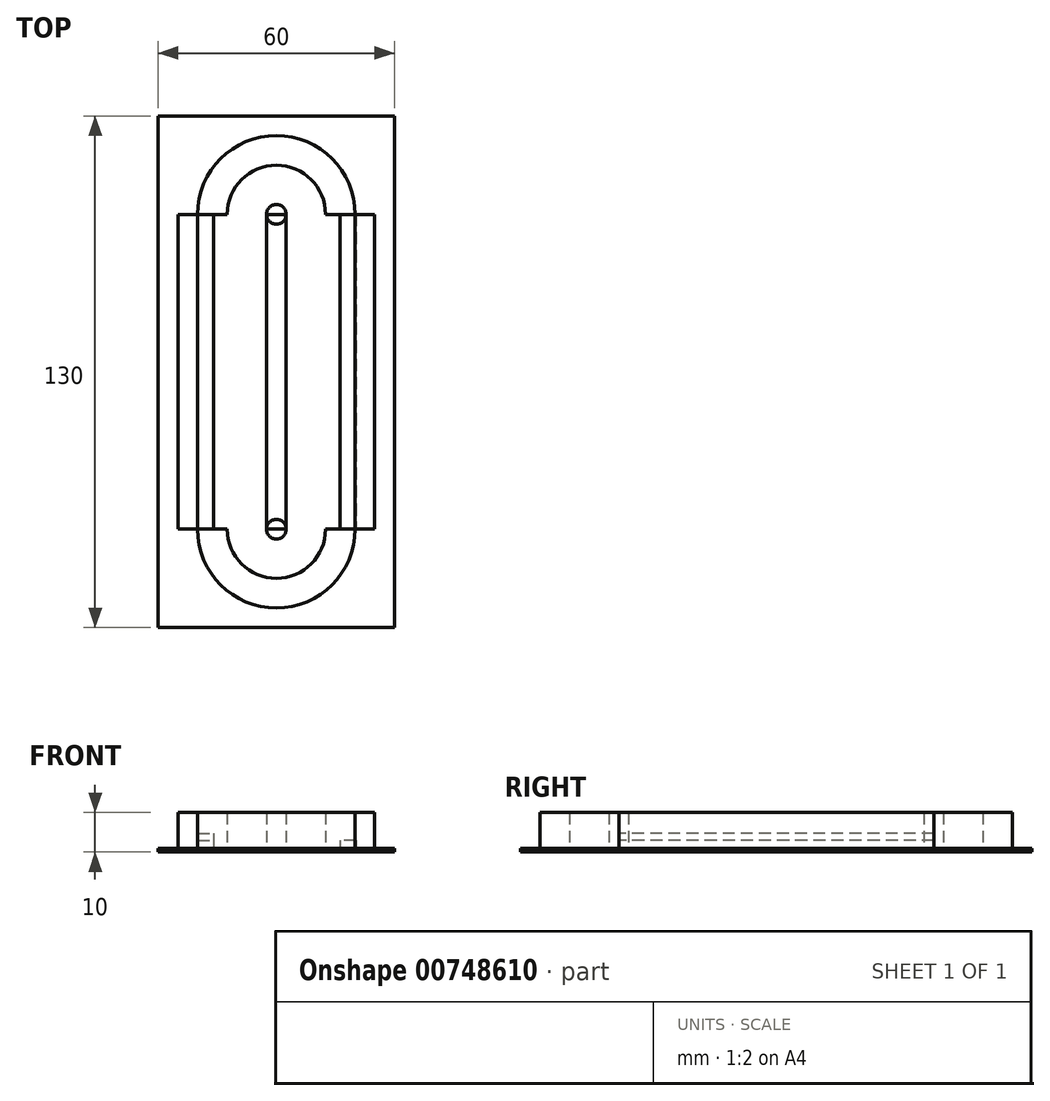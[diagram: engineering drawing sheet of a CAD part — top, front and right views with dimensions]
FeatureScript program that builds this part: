
annotation { "Feature Type Name" : "Feature", "Feature Type Description" : "" }
export const myFeature = defineFeature(function(context is Context, id is Id, definition is map)
    precondition{}
    {
        {
            var Q0;
            Q0=qCreatedBy(makeId("Top.planeOp"),FACE);
            var sketch = newSketch(context, id + "F0", { "sketchPlane" : qUnion([Q0])});
            skLineSegment(sketch, "E0", {"start": v(0, 0) * mm, "end": v(0, 40) * mm});
            skLineSegment(sketch, "E1", {"start": v(0, 40) * mm, "end": v(0, -40) * mm});
            skLineSegment(sketch, "E2", {"start": v(0, -40) * mm, "end": v(0, 0) * mm});
            skCircle(sketch, "E3", {"center": v(0, 40) * mm, "radius": 12.5 * mm});
            skCircle(sketch, "E4", {"center": v(0, -40) * mm, "radius": 12.5 * mm});
            skLineSegment(sketch, "E5", {"start": v(0, -40) * mm, "end": v(-12.5, -40) * mm});
            skLineSegment(sketch, "E6", {"start": v(-12.5, -40) * mm, "end": v(12.5, -40) * mm});
            skLineSegment(sketch, "E7", {"start": v(0, 38.18) * mm, "end": v(0, 40) * mm});
            skLineSegment(sketch, "E8", {"start": v(0, 40) * mm, "end": v(12.5, 40) * mm});
            skLineSegment(sketch, "E9", {"start": v(12.5, 40) * mm, "end": v(-12.5, 40) * mm});
            skLineSegment(sketch, "E10", {"start": v(-12.5, 40) * mm, "end": v(-12.5, -40) * mm});
            skLineSegment(sketch, "E11", {"start": v(12.5, -40) * mm, "end": v(12.5, 40) * mm});
            skCircle(sketch, "E12", {"center": v(0, 40) * mm, "radius": 20 * mm});
            skCircle(sketch, "E13", {"center": v(0, -40) * mm, "radius": 20 * mm});
            skLineSegment(sketch, "E14", {"start": v(14.46, -40) * mm, "end": v(20, -40) * mm});
            skLineSegment(sketch, "E15", {"start": v(20, -40) * mm, "end": v(-20, -40) * mm});
            skLineSegment(sketch, "E16", {"start": v(-20, -40) * mm, "end": v(-20, 40) * mm});
            skLineSegment(sketch, "E17", {"start": v(20, -40) * mm, "end": v(20, 40) * mm});
            skLineSegment(sketch, "E18", {"start": v(20, 40) * mm, "end": v(12.5, 40) * mm});
            skLineSegment(sketch, "E19", {"start": v(-12.5, 40) * mm, "end": v(-20, 40) * mm});
            skLineSegment(sketch, "E20", {"start": v(-20, 40) * mm, "end": v(20, 40) * mm});
            skLineSegment(sketch, "E21", {"start": v(20, 40) * mm, "end": v(25, 40) * mm});
            skLineSegment(sketch, "E22", {"start": v(25, 40) * mm, "end": v(25, -40) * mm});
            skLineSegment(sketch, "E23", {"start": v(25, -40) * mm, "end": v(20, -40) * mm});
            skLineSegment(sketch, "E24", {"start": v(-20, -40) * mm, "end": v(-25, -40) * mm});
            skLineSegment(sketch, "E25", {"start": v(-25, -40) * mm, "end": v(-25, 40) * mm});
            skLineSegment(sketch, "E26", {"start": v(-25, 40) * mm, "end": v(-20, 40) * mm});
            skArc(sketch, "E27", {"start": v(-12.5, -40) * mm, "mid": v(0, -52.5) * mm, "end": v(12.5, -40) * mm});
            skSolve(sketch);
        }
        {
            var Q0;
            Q0=qCreatedBy(makeId("Top.planeOp"),FACE);
            var sketch = newSketch(context, id + "F1", { "sketchPlane" : qUnion([Q0])});
            skLineSegment(sketch, "E28", {"start": v(0, 0) * mm, "end": v(0, 40) * mm});
            skLineSegment(sketch, "E29", {"start": v(0, -40) * mm, "end": v(2.5, -40) * mm});
            skLineSegment(sketch, "E30", {"start": v(2.5, -40) * mm, "end": v(-2.5, -40) * mm});
            skLineSegment(sketch, "E31", {"start": v(-2.5, -40) * mm, "end": v(-2.5, 40) * mm});
            skLineSegment(sketch, "E32", {"start": v(-2.5, 40) * mm, "end": v(2.5, 40) * mm});
            skLineSegment(sketch, "E33", {"start": v(2.5, 40) * mm, "end": v(2.5, -40) * mm});
            skCircle(sketch, "E34", {"center": v(0, 40) * mm, "radius": 2.5 * mm});
            skCircle(sketch, "E35", {"center": v(0, -40) * mm, "radius": 2.5 * mm});
            skSolve(sketch);
        }
        {
            var Q0;
            {var subQ0=sQuery(id+"F0.wireOp",EDGE,"E18");Q0=makeQuery(id+"F0.imprint","IMPRINT",FACE,{"disambiguationData":[TD([[makeQuery(id+"F0.imprint","IMPRINT",EDGE,{"derivedFrom":subQ0}),-1.0]])]});}
            var Q1;
            {var subQ3=sQuery(id+"F0.wireOp",EDGE,"E14");Q1=makeQuery(id+"F0.imprint","IMPRINT",FACE,{"disambiguationData":[TD([[makeQuery(id+"F0.imprint","IMPRINT",EDGE,{"derivedFrom":subQ3}),-1.0]])]});}
            var Q2;
            Q2=makeQuery(id+"F0.imprint","IMPRINT",FACE,{"disambiguationData":[TD([[makeQuery(id+"F0.imprint","IMPRINT",EDGE,{"derivedFrom":sQuery(id+"F0.wireOp",EDGE,"E17")}),-1.0]])]});
            var Q3;
            Q3=makeQuery(id+"F0.imprint","IMPRINT",FACE,{"disambiguationData":[TD([[makeQuery(id+"F0.imprint","IMPRINT",EDGE,{"derivedFrom":sQuery(id+"F0.wireOp",EDGE,"E16")}),1.0]])]});
            var Q4;
            {var subQ4=sQuery(id+"F1.wireOp",EDGE,"E31");Q4=makeQuery(id+"F1.imprint","IMPRINT",FACE,{"disambiguationData":[TD([[makeQuery(id+"F1.imprint","IMPRINT",EDGE,{"derivedFrom":subQ4}),-1.0]])]});}
            var Q5;
            {var subQ0=sQuery(id+"F1.wireOp",EDGE,"E29");Q5=makeQuery(id+"F1.imprint","IMPRINT",FACE,{"disambiguationData":[TD([[makeQuery(id+"F1.imprint","IMPRINT",EDGE,{"derivedFrom":subQ0}),-1.0]])]});}
            var Q6;
            {var subQ0=sQuery(id+"F1.wireOp",EDGE,"E32");var subQ1=makeQuery(id+"F1.imprint","INTERSECT",VERTEX,{"derivedFrom":[sQuery(id+"F1.wireOp",EDGE,"E28"),subQ0]});Q6=makeQuery(id+"F1.imprint","IMPRINT",FACE,{"disambiguationData":[TD([[makeQuery(id+"F1.imprint","IMPRINT",EDGE,{"disambiguationData":[TD([[subQ1,-1.0]])],"derivedFrom":subQ0}),1.0]])]});}
            extrude(context, id + "F2", {"entities" : qUnion([Q0, Q1, Q2, Q3, Q4, Q5, Q6]), "depth" : 10 * mm, "offsetDistance" : 25 * mm});
        }
        {
            var Q0;
            Q0=qCreatedBy(makeId("Top.planeOp"),FACE);
            var sketch = newSketch(context, id + "F3", { "sketchPlane" : qUnion([Q0])});
            skLineSegment(sketch, "E36", {"start": v(0, 0) * mm, "end": v(25, 0) * mm});
            skLineSegment(sketch, "E37", {"start": v(0, 0) * mm, "end": v(-25, 0) * mm});
            skLineSegment(sketch, "E38", {"start": v(0, 0) * mm, "end": v(0, -60) * mm});
            skLineSegment(sketch, "E39", {"start": v(0, -60) * mm, "end": v(-25, -60) * mm});
            skLineSegment(sketch, "E40", {"start": v(-25, -60) * mm, "end": v(-25, 0) * mm});
            skLineSegment(sketch, "E41", {"start": v(0, -60) * mm, "end": v(25, -60) * mm});
            skLineSegment(sketch, "E42", {"start": v(25, -60) * mm, "end": v(25, 0) * mm});
            skLineSegment(sketch, "E43", {"start": v(0, 0) * mm, "end": v(0, 60) * mm});
            skLineSegment(sketch, "E44", {"start": v(0, 60) * mm, "end": v(25, 60) * mm});
            skLineSegment(sketch, "E45", {"start": v(25, 60) * mm, "end": v(25, 0) * mm});
            skLineSegment(sketch, "E46", {"start": v(0, 60) * mm, "end": v(-25, 60) * mm});
            skLineSegment(sketch, "E47", {"start": v(-25, 60) * mm, "end": v(-25, 0) * mm});
            skLineSegment(sketch, "E48.bottom", {"start": v(-25, 60) * mm, "end": v(25, 60) * mm});
            skLineSegment(sketch, "E48.top", {"start": v(-25, -60) * mm, "end": v(25, -60) * mm});
            skLineSegment(sketch, "E48.left", {"start": v(-25, 60) * mm, "end": v(-25, -60) * mm});
            skLineSegment(sketch, "E48.right", {"start": v(25, 60) * mm, "end": v(25, -60) * mm});
            skLineSegment(sketch, "E49", {"start": v(0, 60) * mm, "end": v(0, 65) * mm});
            skLineSegment(sketch, "E50", {"start": v(0, 65) * mm, "end": v(-25, 65) * mm});
            skLineSegment(sketch, "E51", {"start": v(-25, 65) * mm, "end": v(0, 65) * mm});
            skLineSegment(sketch, "E52", {"start": v(0, 65) * mm, "end": v(25, 65) * mm});
            skLineSegment(sketch, "E53", {"start": v(25, 0) * mm, "end": v(30, 0) * mm});
            skLineSegment(sketch, "E54", {"start": v(30, 0) * mm, "end": v(30, 65) * mm});
            skLineSegment(sketch, "E55", {"start": v(30, 65) * mm, "end": v(25, 65) * mm});
            skLineSegment(sketch, "E56", {"start": v(30, 0) * mm, "end": v(30, -65) * mm});
            skLineSegment(sketch, "E57", {"start": v(30, -65) * mm, "end": v(-25, -65) * mm});
            skLineSegment(sketch, "E58", {"start": v(-25, -65) * mm, "end": v(-30, -65) * mm});
            skLineSegment(sketch, "E59", {"start": v(-30, -65) * mm, "end": v(-30, 65) * mm});
            skLineSegment(sketch, "E60", {"start": v(-30, 65) * mm, "end": v(-25, 65) * mm});
            skSolve(sketch);
        }
        {
            var Q0;
            {Q0=qUnion([makeQuery(id+"F3.imprint","IMPRINT",FACE,{"disambiguationData":[TD([[makeQuery(id+"F3.imprint","IMPRINT",EDGE,{"derivedFrom":sQuery(id+"F3.wireOp",EDGE,"E44")}),1.0]])]}),makeQuery(id+"F3.imprint","IMPRINT",FACE,{"disambiguationData":[TD([[makeQuery(id+"F3.imprint","IMPRINT",EDGE,{"derivedFrom":sQuery(id+"F3.wireOp",EDGE,"E39")}),1.0]])]})]);}
            var Q1;
            Q1=makeQuery(id+"F3.imprint","IMPRINT",FACE,{"disambiguationData":[TD([[makeQuery(id+"F3.imprint","IMPRINT",EDGE,{"derivedFrom":sQuery(id+"F3.wireOp",EDGE,"E37")}),1.0]])]});
            var Q2;
            Q2=makeQuery(id+"F3.imprint","IMPRINT",FACE,{"disambiguationData":[TD([[makeQuery(id+"F3.imprint","IMPRINT",EDGE,{"derivedFrom":sQuery(id+"F3.wireOp",EDGE,"E37")}),-1.0]])]});
            var Q3;
            Q3=makeQuery(id+"F3.imprint","IMPRINT",FACE,{"disambiguationData":[TD([[makeQuery(id+"F3.imprint","IMPRINT",EDGE,{"derivedFrom":sQuery(id+"F3.wireOp",EDGE,"E36")}),1.0]])]});
            var Q4;
            Q4=makeQuery(id+"F3.imprint","IMPRINT",FACE,{"disambiguationData":[TD([[makeQuery(id+"F3.imprint","IMPRINT",EDGE,{"derivedFrom":sQuery(id+"F3.wireOp",EDGE,"E36")}),-1.0]])]});
            extrude(context, id + "F4", {"entities" : qUnion([Q0, Q1, Q2, Q3, Q4]), "depth" : 0.9 * mm, "offsetDistance" : 25 * mm});
        }
        {
            var Q0;
            Q0=makeQuery(id+"F4.opExtrude","CAP_FACE",FACE,{"disambiguationData":[OSD([sQuery(id+"F3.wireOp",EDGE,"E50"),sQuery(id+"F3.wireOp",EDGE,"E52"),sQuery(id+"F3.wireOp",EDGE,"E54"),sQuery(id+"F3.wireOp",EDGE,"E55"),sQuery(id+"F3.wireOp",EDGE,"E56"),sQuery(id+"F3.wireOp",EDGE,"E57"),sQuery(id+"F3.wireOp",EDGE,"E58"),sQuery(id+"F3.wireOp",EDGE,"E59"),sQuery(id+"F3.wireOp",EDGE,"E60")])],"isStart":false});
            var sketch = newSketch(context, id + "F5", { "sketchPlane" : qUnion([Q0])});
            skLineSegment(sketch, "E61.bottom", {"start": v(-20, 40) * mm, "end": v(-16, 40) * mm});
            skLineSegment(sketch, "E61.top", {"start": v(-20, -40) * mm, "end": v(-16, -40) * mm});
            skLineSegment(sketch, "E61.left", {"start": v(-20, 40) * mm, "end": v(-20, -40) * mm});
            skLineSegment(sketch, "E61.right", {"start": v(-16, 40) * mm, "end": v(-16, -40) * mm});
            skLineSegment(sketch, "E62.bottom", {"start": v(20.25, 40.1) * mm, "end": v(16.25, 40.1) * mm});
            skLineSegment(sketch, "E62.top", {"start": v(20.25, -39.9) * mm, "end": v(16.25, -39.9) * mm});
            skLineSegment(sketch, "E62.left", {"start": v(20.25, 40.1) * mm, "end": v(20.25, -39.9) * mm});
            skLineSegment(sketch, "E62.right", {"start": v(16.25, 40.1) * mm, "end": v(16.25, -39.9) * mm});
            skSolve(sketch);
        }
        {
            var Q0;
            Q0=makeQuery(id+"F5.imprint","IMPRINT",FACE,{"disambiguationData":[TD([[makeQuery(id+"F5.imprint","IMPRINT",EDGE,{"derivedFrom":sQuery(id+"F5.wireOp",EDGE,"E62.bottom")}),1.0]])]});
            var Q1;
            Q1=makeQuery(id+"F5.imprint","IMPRINT",FACE,{"disambiguationData":[TD([[makeQuery(id+"F5.imprint","IMPRINT",EDGE,{"derivedFrom":sQuery(id+"F5.wireOp",EDGE,"E61.bottom")}),-1.0]])]});
            extrude(context, id + "F6", {"entities" : qUnion([Q0, Q1]), "depth" : 2.1 * mm, "offsetDistance" : 25 * mm});
        }
        {
            var Q0;
            Q0=makeQuery(id+"F6.opExtrude","CAP_FACE",FACE,{"disambiguationData":[OSD([sQuery(id+"F5.wireOp",EDGE,"E61.bottom"),sQuery(id+"F5.wireOp",EDGE,"E61.top"),sQuery(id+"F5.wireOp",EDGE,"E61.left"),sQuery(id+"F5.wireOp",EDGE,"E61.right")])],"isStart":false});
            var sketch = newSketch(context, id + "F7", { "sketchPlane" : qUnion([Q0])});
            skLineSegment(sketch, "E63", {"start": v(-20, -40) * mm, "end": v(-16, -40) * mm});
            skLineSegment(sketch, "E64", {"start": v(-16, -40) * mm, "end": v(-18, -40) * mm});
            skLineSegment(sketch, "E65", {"start": v(-18, -40) * mm, "end": v(-18, 40) * mm});
            skLineSegment(sketch, "E66", {"start": v(-18, 40) * mm, "end": v(-20, 40) * mm});
            skLineSegment(sketch, "E67", {"start": v(-20, 40) * mm, "end": v(-18, 40) * mm});
            skLineSegment(sketch, "E68", {"start": v(-20, 40) * mm, "end": v(-20, -40) * mm});
            skSolve(sketch);
        }
        {
            var Q0;
            Q0=makeQuery(id+"F6.opExtrude","CAP_FACE",FACE,{"disambiguationData":[OSD([sQuery(id+"F5.wireOp",EDGE,"E62.bottom"),sQuery(id+"F5.wireOp",EDGE,"E62.top"),sQuery(id+"F5.wireOp",EDGE,"E62.left"),sQuery(id+"F5.wireOp",EDGE,"E62.right")])],"isStart":false});
            var sketch = newSketch(context, id + "F8", { "sketchPlane" : qUnion([Q0])});
            skLineSegment(sketch, "E69", {"start": v(16.25, -39.9) * mm, "end": v(20.25, -39.9) * mm});
            skLineSegment(sketch, "E70", {"start": v(20.25, -39.9) * mm, "end": v(18.25, -39.9) * mm});
            skLineSegment(sketch, "E71", {"start": v(18.25, -39.9) * mm, "end": v(18.25, 40.1) * mm});
            skLineSegment(sketch, "E72", {"start": v(18.25, 40.1) * mm, "end": v(20.25, 40.1) * mm});
            skLineSegment(sketch, "E73", {"start": v(20.25, 40.1) * mm, "end": v(20.25, -39.9) * mm});
            skSolve(sketch);
        }
        {
            var Q0;
            Q0=makeQuery(id+"F8.imprint","IMPRINT",FACE,{"disambiguationData":[TD([[makeQuery(id+"F8.imprint","IMPRINT",EDGE,{"derivedFrom":sQuery(id+"F8.wireOp",EDGE,"E70")}),-1.0]])]});
            var Q1;
            Q1=makeQuery(id+"F7.imprint","IMPRINT",FACE,{"disambiguationData":[TD([[makeQuery(id+"F7.imprint","IMPRINT",EDGE,{"derivedFrom":sQuery(id+"F7.wireOp",EDGE,"E63")}),1.0]])]});
            extrude(context, id + "F9", {"entities" : qUnion([Q0, Q1]), "depth" : 1.7 * mm, "offsetDistance" : 25 * mm});
        }
    });
